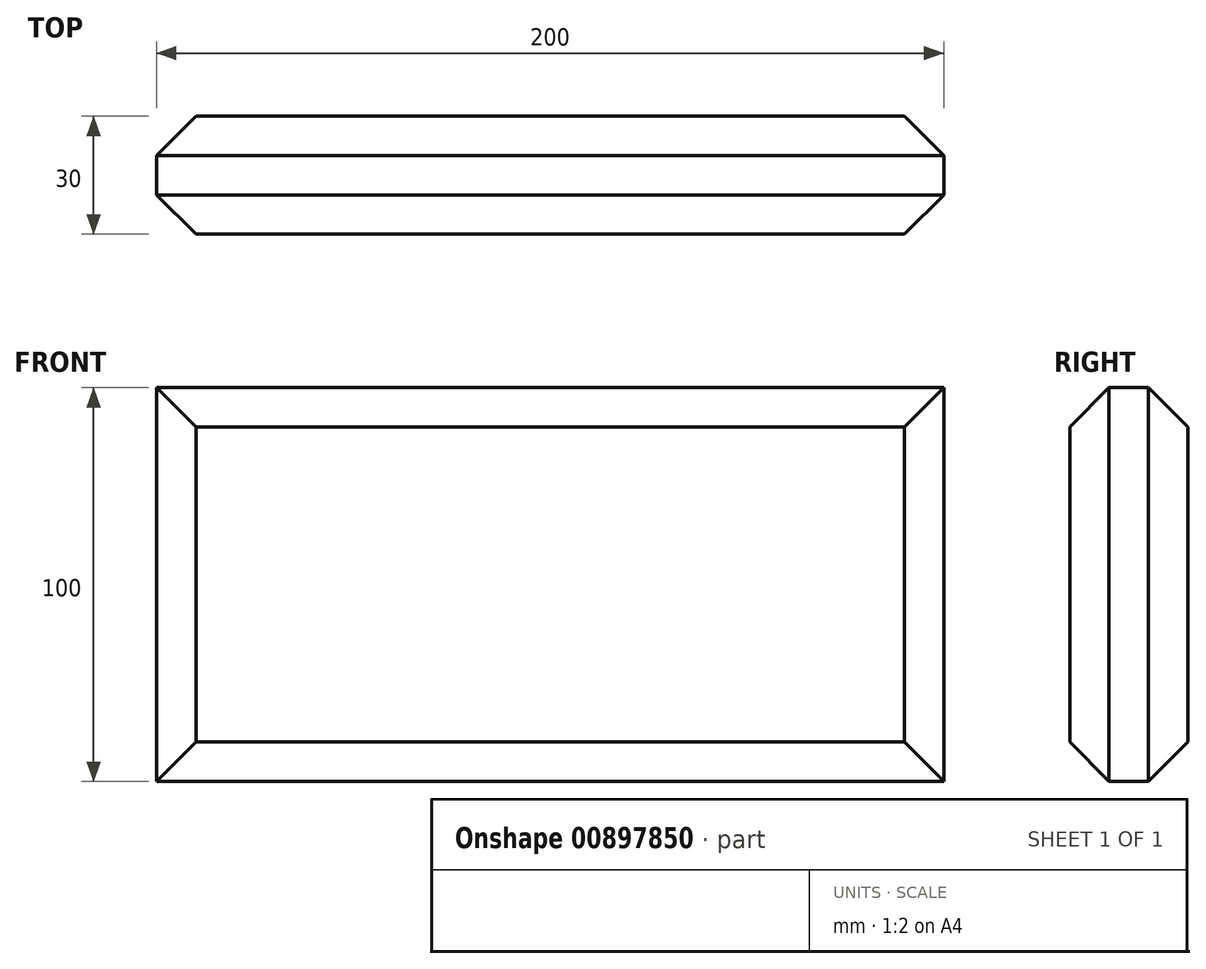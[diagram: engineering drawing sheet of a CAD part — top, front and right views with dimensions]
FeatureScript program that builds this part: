
annotation { "Feature Type Name" : "Feature", "Feature Type Description" : "" }
export const myFeature = defineFeature(function(context is Context, id is Id, definition is map)
    precondition{}
    {
        {
            var Q0;
            Q0=qCreatedBy(makeId("Front.planeOp"),FACE);
            var sketch = newSketch(context, id + "F0", { "sketchPlane" : qUnion([Q0])});
            skLineSegment(sketch, "E0.bottom", {"start": v(-100, 50) * mm, "end": v(100, 50) * mm});
            skLineSegment(sketch, "E0.top", {"start": v(-100, -50) * mm, "end": v(100, -50) * mm});
            skLineSegment(sketch, "E0.left", {"start": v(-100, 50) * mm, "end": v(-100, -50) * mm});
            skLineSegment(sketch, "E0.right", {"start": v(100, 50) * mm, "end": v(100, -50) * mm});
            skPoint(sketch, "E0.middle", {"position": v(0, 0) * mm});
            skSolve(sketch);
        }
        {
            var Q0;
            Q0 = qSketchRegion(id + "F0", true);
            extrude(context, id + "F1", {"entities" : qUnion([Q0]), "depth" : 30 * mm, "offsetDistance" : 25.4 * mm});
        }
        {
            var Q0;
            Q0=makeQuery(id+"F1.opExtrude","CAP_EDGE",EDGE,{"disambiguationData":[OSD([sQuery(id+"F0.wireOp",EDGE,"E0.bottom")])],"isStart":false});
            chamfer(context, id + "F2", {"entities" : qUnion([Q0]), "width" : 10 * mm, "tangentPropagation" : true});
        }
        {
            var Q0;
            Q0=makeQuery(id+"F1.opExtrude","CAP_EDGE",EDGE,{"disambiguationData":[OSD([sQuery(id+"F0.wireOp",EDGE,"E0.bottom")])],"isStart":true});
            chamfer(context, id + "F3", {"entities" : qUnion([Q0]), "width" : 10 * mm, "tangentPropagation" : true});
        }
        {
            var Q0;
            Q0=makeQuery(id+"F1.opExtrude","CAP_EDGE",EDGE,{"disambiguationData":[OSD([sQuery(id+"F0.wireOp",EDGE,"E0.top")])],"isStart":false});
            chamfer(context, id + "F4", {"entities" : qUnion([Q0]), "width" : 10 * mm, "tangentPropagation" : true});
        }
        {
            var Q0;
            Q0=makeQuery(id+"F1.opExtrude","CAP_EDGE",EDGE,{"disambiguationData":[OSD([sQuery(id+"F0.wireOp",EDGE,"E0.top")])],"isStart":true});
            chamfer(context, id + "F5", {"entities" : qUnion([Q0]), "width" : 10 * mm, "tangentPropagation" : true});
        }
        {
            var Q0;
            Q0=makeQuery(id+"F1.opExtrude","CAP_EDGE",EDGE,{"disambiguationData":[OSD([sQuery(id+"F0.wireOp",EDGE,"E0.left")])],"isStart":false});
            chamfer(context, id + "F6", {"entities" : qUnion([Q0]), "width" : 10 * mm, "tangentPropagation" : true});
        }
        {
            var Q0;
            Q0=makeQuery(id+"F1.opExtrude","CAP_EDGE",EDGE,{"disambiguationData":[OSD([sQuery(id+"F0.wireOp",EDGE,"E0.right")])],"isStart":false});
            chamfer(context, id + "F7", {"entities" : qUnion([Q0]), "width" : 10 * mm, "tangentPropagation" : true});
        }
        {
            var Q0;
            Q0=makeQuery(id+"F1.opExtrude","CAP_EDGE",EDGE,{"disambiguationData":[OSD([sQuery(id+"F0.wireOp",EDGE,"E0.left")])],"isStart":true});
            chamfer(context, id + "F8", {"entities" : qUnion([Q0]), "width" : 10 * mm, "tangentPropagation" : true});
        }
        {
            var Q0;
            Q0=makeQuery(id+"F1.opExtrude","CAP_EDGE",EDGE,{"disambiguationData":[OSD([sQuery(id+"F0.wireOp",EDGE,"E0.right")])],"isStart":true});
            chamfer(context, id + "F9", {"entities" : qUnion([Q0]), "width" : 10 * mm, "tangentPropagation" : true});
        }
    });
